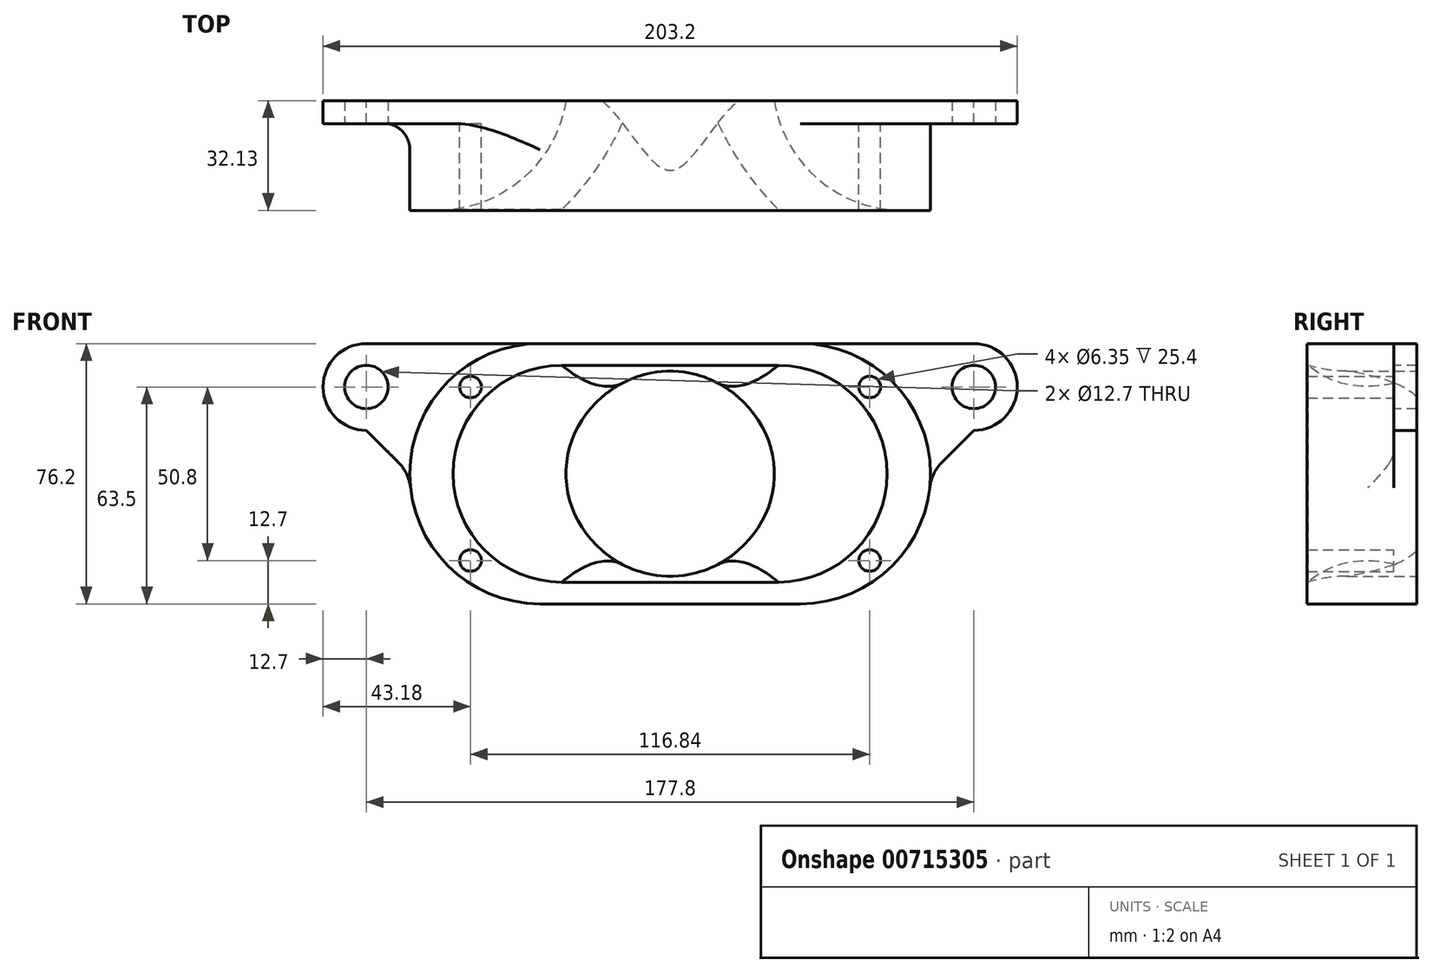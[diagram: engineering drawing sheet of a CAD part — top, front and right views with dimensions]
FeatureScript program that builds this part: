
annotation { "Feature Type Name" : "Feature", "Feature Type Description" : "" }
export const myFeature = defineFeature(function(context is Context, id is Id, definition is map)
    precondition{}
    {
        {
            var Q0;
            Q0=qCreatedBy(makeId("Front.planeOp"),FACE);
            var sketch = newSketch(context, id + "F0", { "sketchPlane" : qUnion([Q0])});
            skCircle(sketch, "E0", {"center": v(-88.9, 25.4) * mm, "radius": 12.7 * mm});
            skCircle(sketch, "E1.MirrorC", {"center": v(88.9, 25.4) * mm, "radius": 12.7 * mm});
            skLineSegment(sketch, "E2", {"start": v(-88.9, 12.7) * mm, "end": v(-79.61, 3.41) * mm});
            skLineSegment(sketch, "E3", {"start": v(79.61, 3.41) * mm, "end": v(88.9, 12.7) * mm});
            skLineSegment(sketch, "E4.top", {"start": v(-38.1, -38.1) * mm, "end": v(38.1, -38.1) * mm});
            skPoint(sketch, "E4.middle", {"position": v(0, 0) * mm});
            skPoint(sketch, "E5.visualSharp", {"position": v(-76.2, -38.1) * mm});
            skArc(sketch, "E5.filletArc", {"start": v(-75.97, -4.17) * mm, "mid": v(-63.52, -28.38) * mm, "end": v(-38.1, -38.1) * mm});
            skPoint(sketch, "E6.visualSharp", {"position": v(76.2, -38.1) * mm});
            skArc(sketch, "E6.filletArc", {"start": v(38.1, -38.1) * mm, "mid": v(63.52, -28.38) * mm, "end": v(75.97, -4.17) * mm});
            skLineSegment(sketch, "E7", {"start": v(-88.9, 38.1) * mm, "end": v(88.9, 38.1) * mm});
            skCircle(sketch, "E8", {"center": v(0, 0) * mm, "radius": 38.1 * mm});
            skPoint(sketch, "E9.visualSharp", {"position": v(-76.2, 0) * mm});
            skArc(sketch, "E9.filletArc", {"start": v(-75.97, -4.17) * mm, "mid": v(-77.15, -0.07) * mm, "end": v(-79.61, 3.41) * mm});
            skPoint(sketch, "E10.visualSharp", {"position": v(76.2, 0) * mm});
            skArc(sketch, "E10.filletArc", {"start": v(79.61, 3.41) * mm, "mid": v(77.15, -0.07) * mm, "end": v(75.97, -4.17) * mm});
            skSolve(sketch);
        }
        {
            var Q0;
            Q0 = qSketchRegion(id + "F0", true);
            extrude(context, id + "F1", {"entities" : qUnion([Q0]), "depth" : 6.35 * mm, "offsetDistance" : 25.4 * mm});
        }
        {
            var Q0;
            Q0=makeQuery(id+"F1.opExtrude","CAP_FACE",FACE,{"disambiguationData":[OSD([sQuery(id+"F0.wireOp",EDGE,"E0"),sQuery(id+"F0.wireOp",EDGE,"E1.MirrorC"),sQuery(id+"F0.wireOp",EDGE,"E2"),sQuery(id+"F0.wireOp",EDGE,"E3"),sQuery(id+"F0.wireOp",EDGE,"E4.top"),sQuery(id+"F0.wireOp",EDGE,"E5.filletArc"),sQuery(id+"F0.wireOp",EDGE,"E6.filletArc"),sQuery(id+"F0.wireOp",EDGE,"E7")])],"isStart":false});
            var sketch = newSketch(context, id + "F2", { "sketchPlane" : qUnion([Q0])});
            skArc(sketch, "E11", {"start": v(-31.75, 31.75) * mm, "mid": v(-63.5, 0) * mm, "end": v(-31.75, -31.75) * mm});
            skArc(sketch, "E12.MirrorC", {"start": v(31.75, 31.75) * mm, "mid": v(63.5, 0) * mm, "end": v(31.75, -31.75) * mm});
            skLineSegment(sketch, "E13", {"start": v(-31.75, 31.75) * mm, "end": v(31.75, 31.75) * mm});
            skLineSegment(sketch, "E14", {"start": v(-31.75, -31.75) * mm, "end": v(31.75, -31.75) * mm});
            skSolve(sketch);
        }
        {
            var Q0;
            Q0=makeQuery(id+"F1.opExtrude","CAP_FACE",FACE,{"disambiguationData":[OSD([sQuery(id+"F0.wireOp",EDGE,"E0"),sQuery(id+"F0.wireOp",EDGE,"E1.MirrorC"),sQuery(id+"F0.wireOp",EDGE,"E2"),sQuery(id+"F0.wireOp",EDGE,"E3"),sQuery(id+"F0.wireOp",EDGE,"E4.top"),sQuery(id+"F0.wireOp",EDGE,"E5.filletArc"),sQuery(id+"F0.wireOp",EDGE,"E6.filletArc"),sQuery(id+"F0.wireOp",EDGE,"E7")])],"isStart":true});
            var sketch = newSketch(context, id + "F3", { "sketchPlane" : qUnion([Q0])});
            skArc(sketch, "E15.0", {"start": v(88.9, 38.1) * mm, "mid": v(101.6, 25.4) * mm, "end": v(88.9, 12.7) * mm});
            skLineSegment(sketch, "E15.1", {"start": v(88.9, 12.7) * mm, "end": v(79.61, 3.41) * mm});
            skLineSegment(sketch, "E15.2", {"start": v(88.9, 38.1) * mm, "end": v(-88.9, 38.1) * mm});
            skArc(sketch, "E15.3", {"start": v(75.97, -4.17) * mm, "mid": v(63.52, -28.38) * mm, "end": v(38.1, -38.1) * mm});
            skArc(sketch, "E15.4", {"start": v(-88.9, 38.1) * mm, "mid": v(-101.6, 25.4) * mm, "end": v(-88.9, 12.7) * mm});
            skLineSegment(sketch, "E15.5", {"start": v(-79.61, 3.41) * mm, "end": v(-88.9, 12.7) * mm});
            skArc(sketch, "E15.6", {"start": v(-38.1, -38.1) * mm, "mid": v(-63.52, -28.38) * mm, "end": v(-75.97, -4.17) * mm});
            skLineSegment(sketch, "E15.7", {"start": v(38.1, -38.1) * mm, "end": v(-38.1, -38.1) * mm});
            skPoint(sketch, "E16.visualSharp", {"position": v(-76.2, 0) * mm});
            skArc(sketch, "E16.filletArc", {"start": v(-75.97, -4.17) * mm, "mid": v(-77.15, -0.07) * mm, "end": v(-79.61, 3.41) * mm});
            skPoint(sketch, "E17.visualSharp", {"position": v(76.2, 0) * mm});
            skArc(sketch, "E17.filletArc", {"start": v(79.61, 3.41) * mm, "mid": v(77.15, -0.07) * mm, "end": v(75.97, -4.17) * mm});
            skSolve(sketch);
        }
        {
            var Q0;
            Q0 = qSketchRegion(id + "F3", true);
            extrude(context, id + "F4", {"entities" : qUnion([Q0]), "operationType" : NewBodyOperationType.ADD, "depth" : 0.38 * mm, "offsetDistance" : 25.4 * mm});
        }
        {
            var Q0;
            Q0=makeQuery(id+"F1.opExtrude","CAP_FACE",FACE,{"disambiguationData":[OSD([sQuery(id+"F0.wireOp",EDGE,"E0"),sQuery(id+"F0.wireOp",EDGE,"E1.MirrorC"),sQuery(id+"F0.wireOp",EDGE,"E2"),sQuery(id+"F0.wireOp",EDGE,"E3"),sQuery(id+"F0.wireOp",EDGE,"E4.top"),sQuery(id+"F0.wireOp",EDGE,"E5.filletArc"),sQuery(id+"F0.wireOp",EDGE,"E6.filletArc"),sQuery(id+"F0.wireOp",EDGE,"E7")])],"isStart":false});
            var sketch = newSketch(context, id + "F5", { "sketchPlane" : qUnion([Q0])});
            skCircle(sketch, "E18", {"center": v(-88.9, 25.4) * mm, "radius": 6.35 * mm});
            skCircle(sketch, "E19", {"center": v(88.9, 25.4) * mm, "radius": 6.35 * mm});
            skSolve(sketch);
        }
        {
            var Q0;
            Q0 = qSketchRegion(id + "F5", true);
            extrude(context, id + "F6", {"entities" : qUnion([Q0]), "operationType" : NewBodyOperationType.REMOVE, "endBound" : BoundingType.THROUGH_ALL, "oppositeDirection" : true, "depth" : 25.4 * mm, "offsetDistance" : 25.4 * mm});
        }
        {
            var Q0;
            Q0=makeQuery(id+"F5.imprint","IMPRINT",FACE,{"disambiguationData":[TD([[makeQuery(id+"F5.imprint","IMPRINT",EDGE,{"derivedFrom":sQuery(id+"F5.wireOp",EDGE,"E18")}),-1.0]])]});
            var sketch = newSketch(context, id + "F7", { "sketchPlane" : qUnion([Q0])});
            skArc(sketch, "E20.0", {"start": v(-76.2, 0) * mm, "mid": v(-65.04, -26.94) * mm, "end": v(-38.1, -38.1) * mm});
            skArc(sketch, "E21.0", {"start": v(38.1, -38.1) * mm, "mid": v(65.04, -26.94) * mm, "end": v(76.2, 0) * mm});
            skLineSegment(sketch, "E22", {"start": v(-38.1, -38.1) * mm, "end": v(38.1, -38.1) * mm});
            skArc(sketch, "E23.MirrorCS", {"start": v(-76.2, 0) * mm, "mid": v(-65.04, 26.94) * mm, "end": v(-38.1, 38.1) * mm});
            skLineSegment(sketch, "E24.MirrorCS", {"start": v(-38.1, 38.1) * mm, "end": v(38.1, 38.1) * mm});
            skArc(sketch, "E25.MirrorCS", {"start": v(38.1, 38.1) * mm, "mid": v(65.04, 26.94) * mm, "end": v(76.2, 0) * mm});
            skCircle(sketch, "E26.0", {"center": v(-58.42, 25.4) * mm, "radius": 3.18 * mm});
            skCircle(sketch, "E27.0", {"center": v(-58.42, -25.4) * mm, "radius": 3.18 * mm});
            skCircle(sketch, "E28.0", {"center": v(58.42, -25.4) * mm, "radius": 3.18 * mm});
            skCircle(sketch, "E29.0", {"center": v(58.42, 25.4) * mm, "radius": 3.18 * mm});
            skSolve(sketch);
        }
        {
            var Q0;
            Q0=makeQuery(id+"F7.imprint","IMPRINT",FACE,{"disambiguationData":[TD([[makeQuery(id+"F7.imprint","IMPRINT",EDGE,{"derivedFrom":sQuery(id+"F7.wireOp",EDGE,"E20.0")}),1.0]])]});
            extrude(context, id + "F8", {"entities" : qUnion([Q0]), "operationType" : NewBodyOperationType.ADD, "depth" : 25.4 * mm, "offsetDistance" : 25.4 * mm});
        }
        {
            var Q0;
            Q0=makeQuery(id+"F4.opExtrude","CAP_FACE",FACE,{"disambiguationData":[OSD([sQuery(id+"F3.wireOp",EDGE,"E15.0"),sQuery(id+"F3.wireOp",EDGE,"E15.1"),sQuery(id+"F3.wireOp",EDGE,"E15.2"),sQuery(id+"F3.wireOp",EDGE,"E15.3"),sQuery(id+"F3.wireOp",EDGE,"E15.4"),sQuery(id+"F3.wireOp",EDGE,"E15.5"),sQuery(id+"F3.wireOp",EDGE,"E15.6"),sQuery(id+"F3.wireOp",EDGE,"E15.7")])],"isStart":false});
            var sketch = newSketch(context, id + "F9", { "sketchPlane" : qUnion([Q0])});
            skCircle(sketch, "E30", {"center": v(0, 0) * mm, "radius": 30 * mm});
            skSolve(sketch);
        }
        {
            var Q0;
            Q0 = qSketchRegion(id + "F9", true);
            extrude(context, id + "F10", {"entities" : qUnion([Q0]), "operationType" : NewBodyOperationType.REMOVE, "oppositeDirection" : true, "depth" : 38.1 * mm, "offsetDistance" : 25.4 * mm});
        }
        {
            var Q0;
            Q0=makeQuery(id+"F8.opExtrude","CAP_FACE",FACE,{"disambiguationData":[OSD([sQuery(id+"F7.wireOp",EDGE,"E20.0"),sQuery(id+"F7.wireOp",EDGE,"E21.0"),sQuery(id+"F7.wireOp",EDGE,"E22"),sQuery(id+"F7.wireOp",EDGE,"E23.MirrorCS"),sQuery(id+"F7.wireOp",EDGE,"E24.MirrorCS"),sQuery(id+"F7.wireOp",EDGE,"E25.MirrorCS"),sQuery(id+"F7.wireOp",EDGE,"E26.0"),sQuery(id+"F7.wireOp",EDGE,"E27.0"),sQuery(id+"F7.wireOp",EDGE,"E28.0"),sQuery(id+"F7.wireOp",EDGE,"E29.0")])],"isStart":false});
            var sketch = newSketch(context, id + "F11", { "sketchPlane" : qUnion([Q0])});
            skArc(sketch, "E31.0", {"start": v(-31.75, 31.75) * mm, "mid": v(-63.5, 0) * mm, "end": v(-31.75, -31.75) * mm});
            skLineSegment(sketch, "E31.1", {"start": v(-31.75, 31.75) * mm, "end": v(31.75, 31.75) * mm});
            skArc(sketch, "E31.2", {"start": v(31.75, 31.75) * mm, "mid": v(63.5, 0) * mm, "end": v(31.75, -31.75) * mm});
            skLineSegment(sketch, "E31.3", {"start": v(-31.75, -31.75) * mm, "end": v(31.75, -31.75) * mm});
            skSolve(sketch);
        }
        {
            var Q0;
            Q0 = qSketchRegion(id + "F11", true);
            extrude(context, id + "F12", {"entities" : qUnion([Q0]), "operationType" : NewBodyOperationType.REMOVE, "oppositeDirection" : true, "depth" : 0.25 * mm, "offsetDistance" : 25.4 * mm});
        }
        {
            var Q0;
            Q0=makeQuery(id+"F12.boolean.opBoolean","INTERSECT",EDGE,{"derivedFrom":[makeQuery(id+"F10.boolean.opBoolean","COPY",FACE,{"derivedFrom":makeQuery(id+"F10.opExtrude","SWEPT_FACE",FACE,{"disambiguationData":[OSD([sQuery(id+"F9.wireOp",EDGE,"E30")])]})}),makeQuery(id+"F12.opExtrude","CAP_FACE",FACE,{"disambiguationData":[OSD([sQuery(id+"F11.wireOp",EDGE,"E31.0"),sQuery(id+"F11.wireOp",EDGE,"E31.1"),sQuery(id+"F11.wireOp",EDGE,"E31.2"),sQuery(id+"F11.wireOp",EDGE,"E31.3")])],"isStart":false})]});
            fillet(context, id + "F13", {"entities" : qUnion([Q0]), "radius" : 38.1 * mm, "tangentPropagation" : true, "allowEdgeOverflow" : false});
        }
        {
            var Q0;
            Q0=makeQuery(id+"F8.opExtrude","CAP_EDGE",EDGE,{"disambiguationData":[OSD([sQuery(id+"F7.wireOp",EDGE,"E20.0"),sQuery(id+"F7.wireOp",EDGE,"E23.MirrorCS")])],"isStart":true});
            var Q1;
            Q1=makeQuery(id+"F8.opExtrude","CAP_EDGE",EDGE,{"disambiguationData":[OSD([sQuery(id+"F7.wireOp",EDGE,"E21.0"),sQuery(id+"F7.wireOp",EDGE,"E25.MirrorCS")])],"isStart":true});
            fillet(context, id + "F14", {"entities" : qUnion([Q0, Q1]), "radius" : 7.62 * mm, "tangentPropagation" : true, "allowEdgeOverflow" : false});
        }
    });
